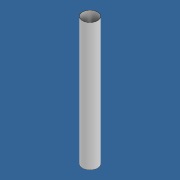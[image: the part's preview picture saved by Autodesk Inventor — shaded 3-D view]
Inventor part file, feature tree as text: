
AUTODESK INVENTOR PART (.ipt)
format: ipt  version: 2021 (Build 250183000, 183)  size: 74,752 bytes
history: native  units: in
note: dims shown in document units (in); Inventor stores cm internally (conversion verified against a paired STEP export)
features: extrude x1, sketch x1
ambient origin geometry x8: Origin, YZ Plane, XZ Plane, XY Plane, X Axis, Y Axis, Z Axis, Center Point
bodies: Solid1 (feature_tree)
feature tree (2):
  extrude  "Extrusion1"  Depth=33.4646in
  sketch  "Sketch1"  dims[d0=4.0157in d1=3.9016in d2=33.4646in d3=0.0in]
